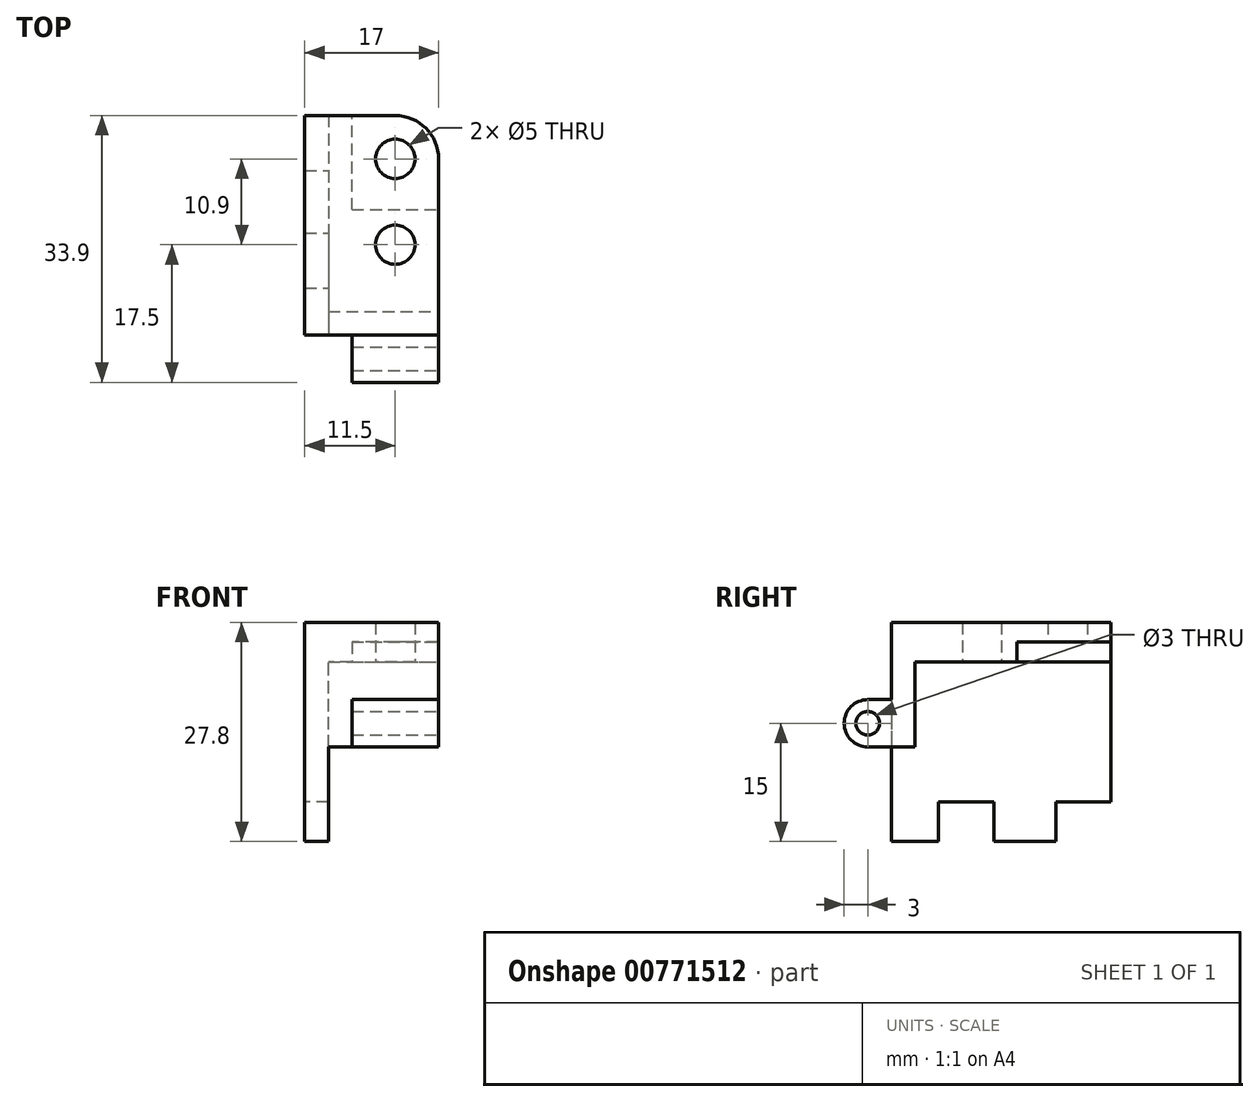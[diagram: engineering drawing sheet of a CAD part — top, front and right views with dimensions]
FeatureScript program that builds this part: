
annotation { "Feature Type Name" : "Feature", "Feature Type Description" : "" }
export const myFeature = defineFeature(function(context is Context, id is Id, definition is map)
    precondition{}
    {
        {
            var Q0;
            Q0=qCreatedBy(makeId("Top.planeOp"),FACE);
            var sketch = newSketch(context, id + "F0", { "sketchPlane" : qUnion([Q0])});
            skCircle(sketch, "E0", {"center": v(0, 0) * mm, "radius": 2.5 * mm});
            skLineSegment(sketch, "E1", {"start": v(0, 0) * mm, "end": v(-2.5, 0) * mm, "construction": true});
            skLineSegment(sketch, "E2", {"start": v(-2.5, 0) * mm, "end": v(2.5, 0) * mm, "construction": true});
            skArc(sketch, "E3", {"start": v(-5.5, 0) * mm, "mid": v(0, -5.5) * mm, "end": v(5.5, 0) * mm});
            skLineSegment(sketch, "E4", {"start": v(-5.5, 0) * mm, "end": v(-5.5, 10.9) * mm});
            skLineSegment(sketch, "E5", {"start": v(-2.5, 10.9) * mm, "end": v(2.5, 10.9) * mm});
            skLineSegment(sketch, "E6", {"start": v(5.5, 10.9) * mm, "end": v(5.5, 0) * mm});
            skCircle(sketch, "E7", {"center": v(0, 10.9) * mm, "radius": 2.5 * mm});
            skArc(sketch, "E8", {"start": v(-5.5, 10.9) * mm, "mid": v(0, 16.4) * mm, "end": v(5.5, 10.9) * mm});
            skLineSegment(sketch, "E9", {"start": v(-5.5, 5.45) * mm, "end": v(-5.5, 4.45) * mm});
            skLineSegment(sketch, "E10", {"start": v(-5.5, 4.45) * mm, "end": v(5.5, 4.45) * mm});
            skLineSegment(sketch, "E11", {"start": v(0, 16.4) * mm, "end": v(-8.5, 16.4) * mm});
            skLineSegment(sketch, "E12", {"start": v(-8.5, 16.4) * mm, "end": v(-8.5, -5.5) * mm});
            skLineSegment(sketch, "E13", {"start": v(-8.5, -5.5) * mm, "end": v(0, -5.5) * mm});
            skLineSegment(sketch, "E14.bottom", {"start": v(-8.5, 16.4) * mm, "end": v(-11.5, 16.4) * mm});
            skLineSegment(sketch, "E14.top", {"start": v(-8.5, -5.5) * mm, "end": v(-11.5, -5.5) * mm});
            skLineSegment(sketch, "E14.right", {"start": v(-11.5, 16.4) * mm, "end": v(-11.5, -5.5) * mm});
            skLineSegment(sketch, "E15", {"start": v(-5.5, 10.9) * mm, "end": v(-5.5, 16.4) * mm});
            skLineSegment(sketch, "E16", {"start": v(5.5, 0) * mm, "end": v(5.5, -8.5) * mm});
            skLineSegment(sketch, "E17", {"start": v(-11.5, -5.5) * mm, "end": v(-11.5, -8.5) * mm});
            skLineSegment(sketch, "E18.bottom", {"start": v(-11.5, -8.5) * mm, "end": v(5.5, -8.5) * mm});
            skLineSegment(sketch, "E18.top", {"start": v(-11.5, -11.5) * mm, "end": v(5.5, -11.5) * mm});
            skLineSegment(sketch, "E18.left", {"start": v(-11.5, -8.5) * mm, "end": v(-11.5, -11.5) * mm});
            skLineSegment(sketch, "E18.right", {"start": v(5.5, -8.5) * mm, "end": v(5.5, -11.5) * mm});
            skLineSegment(sketch, "E19", {"start": v(-8.5, -5.5) * mm, "end": v(-8.5, -8.5) * mm});
            skLineSegment(sketch, "E20", {"start": v(-8.5, -8.5) * mm, "end": v(-8.5, -11.5) * mm});
            skSolve(sketch);
        }
        {
            var Q0;
            Q0=makeQuery(id+"F0.imprint","IMPRINT",FACE,{"disambiguationData":[TD([[makeQuery(id+"F0.imprint","IMPRINT",EDGE,{"derivedFrom":sQuery(id+"F0.wireOp",EDGE,"E0")}),-1.0]])]});
            var Q1;
            {var subQ7=sQuery(id+"F0.wireOp",EDGE,"E10");Q1=makeQuery(id+"F0.imprint","IMPRINT",FACE,{"disambiguationData":[TD([[makeQuery(id+"F0.imprint","IMPRINT",EDGE,{"derivedFrom":subQ7}),1.0]])]});}
            var Q2;
            {var subQ3=sQuery(id+"F0.wireOp",EDGE,"E12");Q2=makeQuery(id+"F0.imprint","IMPRINT",FACE,{"disambiguationData":[TD([[makeQuery(id+"F0.imprint","IMPRINT",EDGE,{"derivedFrom":subQ3}),1.0]])]});}
            var Q3;
            {var subQ0=sQuery(id+"F0.wireOp",EDGE,"E15");Q3=makeQuery(id+"F0.imprint","IMPRINT",FACE,{"disambiguationData":[TD([[makeQuery(id+"F0.imprint","IMPRINT",EDGE,{"derivedFrom":subQ0}),-1.0]])]});}
            var Q4;
            {var subQ4=sQuery(id+"F0.wireOp",EDGE,"E13");Q4=makeQuery(id+"F0.imprint","IMPRINT",FACE,{"disambiguationData":[TD([[makeQuery(id+"F0.imprint","IMPRINT",EDGE,{"derivedFrom":subQ4}),-1.0]])]});}
            var Q5;
            {var subQ0=sQuery(id+"F0.wireOp",EDGE,"E18.right");var subQ7=sQuery(id+"F0.wireOp",EDGE,"E18.left");Q5=qUnion([makeQuery(id+"F0.imprint","IMPRINT",FACE,{"disambiguationData":[TD([[makeQuery(id+"F0.imprint","IMPRINT",EDGE,{"derivedFrom":subQ7}),1.0]])]}),makeQuery(id+"F0.imprint","IMPRINT",FACE,{"disambiguationData":[TD([[makeQuery(id+"F0.imprint","IMPRINT",EDGE,{"derivedFrom":subQ0}),-1.0]])]})]);}
            extrude(context, id + "F1", {"entities" : qUnion([Q0, Q1, Q2, Q3, Q4, Q5]), "depth" : 5 * mm, "offsetDistance" : 25 * mm});
        }
        {
            var Q0;
            {var subQ7=sQuery(id+"F0.wireOp",EDGE,"E10");Q0=makeQuery(id+"F0.imprint","IMPRINT",FACE,{"disambiguationData":[TD([[makeQuery(id+"F0.imprint","IMPRINT",EDGE,{"derivedFrom":subQ7}),1.0]])]});}
            var Q1;
            {var subQ0=sQuery(id+"F0.wireOp",EDGE,"E15");Q1=makeQuery(id+"F0.imprint","IMPRINT",FACE,{"disambiguationData":[TD([[makeQuery(id+"F0.imprint","IMPRINT",EDGE,{"derivedFrom":subQ0}),-1.0]])]});}
            extrude(context, id + "F2", {"entities" : qUnion([Q0, Q1]), "operationType" : NewBodyOperationType.REMOVE, "depth" : 2.5 * mm, "offsetDistance" : 25 * mm});
        }
        {
            var Q0;
            {var subQ0=sQuery(id+"F0.wireOp",EDGE,"E18.left");Q0=makeQuery(id+"F0.imprint","IMPRINT",FACE,{"disambiguationData":[TD([[makeQuery(id+"F0.imprint","IMPRINT",EDGE,{"derivedFrom":subQ0}),1.0]])]});}
            var Q1;
            Q1=makeQuery(id+"F0.imprint","IMPRINT",FACE,{"disambiguationData":[TD([[makeQuery(id+"F0.imprint","IMPRINT",EDGE,{"derivedFrom":sQuery(id+"F0.wireOp",EDGE,"E12")}),-1.0]])]});
            var Q2;
            Q2=makeQuery(id+"F0.imprint","IMPRINT",FACE,{"disambiguationData":[TD([[makeQuery(id+"F0.imprint","IMPRINT",EDGE,{"derivedFrom":sQuery(id+"F0.wireOp",EDGE,"E14.top")}),1.0]])]});
            extrude(context, id + "F3", {"entities" : qUnion([Q0, Q1, Q2]), "operationType" : NewBodyOperationType.ADD, "oppositeDirection" : true, "depth" : 22.8 * mm, "offsetDistance" : 25 * mm, "hasSecondDirection" : true, "secondDirectionOppositeDirection" : false, "secondDirectionDepth" : 5 * mm});
        }
        {
            var Q0;
            Q0=makeQuery(id+"F3.opExtrude","CAP_FACE",FACE,{"disambiguationData":[OSD([sQuery(id+"F0.wireOp",EDGE,"E12"),sQuery(id+"F0.wireOp",EDGE,"E14.bottom"),sQuery(id+"F0.wireOp",EDGE,"E14.right"),sQuery(id+"F0.wireOp",EDGE,"E17"),sQuery(id+"F0.wireOp",EDGE,"E18.top"),sQuery(id+"F0.wireOp",EDGE,"E18.left"),sQuery(id+"F0.wireOp",EDGE,"E19"),sQuery(id+"F0.wireOp",EDGE,"E20")])],"isStart":false});
            var sketch = newSketch(context, id + "F4", { "sketchPlane" : qUnion([Q0])});
            skLineSegment(sketch, "E21.bottom", {"start": v(-11.5, 5.5) * mm, "end": v(-8.5, 5.5) * mm});
            skLineSegment(sketch, "E21.top", {"start": v(-11.5, -1.5) * mm, "end": v(-8.5, -1.5) * mm});
            skLineSegment(sketch, "E21.left", {"start": v(-11.5, 5.5) * mm, "end": v(-11.5, -1.5) * mm});
            skLineSegment(sketch, "E21.right", {"start": v(-8.5, 5.5) * mm, "end": v(-8.5, -1.5) * mm});
            skLineSegment(sketch, "E22.bottom", {"start": v(-11.5, -16.4) * mm, "end": v(-8.5, -16.4) * mm});
            skLineSegment(sketch, "E22.top", {"start": v(-11.5, -9.4) * mm, "end": v(-8.5, -9.4) * mm});
            skLineSegment(sketch, "E22.left", {"start": v(-11.5, -16.4) * mm, "end": v(-11.5, -9.4) * mm});
            skLineSegment(sketch, "E22.right", {"start": v(-8.5, -16.4) * mm, "end": v(-8.5, -9.4) * mm});
            skSolve(sketch);
        }
        {
            var Q0;
            Q0=makeQuery(id+"F4.imprint","IMPRINT",FACE,{"disambiguationData":[TD([[makeQuery(id+"F4.imprint","IMPRINT",EDGE,{"derivedFrom":sQuery(id+"F4.wireOp",EDGE,"E22.bottom")}),-1.0]])]});
            var Q1;
            Q1=makeQuery(id+"F4.imprint","IMPRINT",FACE,{"disambiguationData":[TD([[makeQuery(id+"F4.imprint","IMPRINT",EDGE,{"derivedFrom":sQuery(id+"F4.wireOp",EDGE,"E21.bottom")}),-1.0]])]});
            extrude(context, id + "F5", {"entities" : qUnion([Q0, Q1]), "operationType" : NewBodyOperationType.REMOVE, "oppositeDirection" : true, "depth" : 5 * mm, "offsetDistance" : 25 * mm});
        }
        {
            var Q0;
            {var subQ0=sQuery(id+"F0.wireOp",EDGE,"E18.right");Q0=makeQuery(id+"F0.imprint","IMPRINT",FACE,{"disambiguationData":[TD([[makeQuery(id+"F0.imprint","IMPRINT",EDGE,{"derivedFrom":subQ0}),-1.0]])]});}
            extrude(context, id + "F6", {"entities" : qUnion([Q0]), "operationType" : NewBodyOperationType.ADD, "oppositeDirection" : true, "depth" : 10.8 * mm, "offsetDistance" : 25 * mm});
        }
        {
            var Q0;
            {var subQ0=sQuery(id+"F0.wireOp",EDGE,"E18.right");Q0=makeQuery(id+"F6.boolean.opBoolean","MERGE",FACE,{"derivedFrom":[makeQuery(id+"F1.opExtrude","SWEPT_FACE",FACE,{"disambiguationData":[OSD([sQuery(id+"F0.wireOp",EDGE,"E6"),sQuery(id+"F0.wireOp",EDGE,"E16"),subQ0])]}),makeQuery(id+"F6.opExtrude","SWEPT_FACE",FACE,{"disambiguationData":[OSD([subQ0])]})]});}
            var sketch = newSketch(context, id + "F7", { "sketchPlane" : qUnion([Q0])});
            skLineSegment(sketch, "E23", {"start": v(-11.5, -10.8) * mm, "end": v(-14.5, -10.8) * mm});
            skLineSegment(sketch, "E24", {"start": v(-14.5, -10.8) * mm, "end": v(-14.5, -7.8) * mm});
            skCircle(sketch, "E25", {"center": v(-14.5, -7.8) * mm, "radius": 1.5 * mm});
            skCircle(sketch, "E26", {"center": v(-14.5, -7.8) * mm, "radius": 3 * mm});
            skLineSegment(sketch, "E27", {"start": v(-14.5, -7.8) * mm, "end": v(-14.5, -4.8) * mm});
            skLineSegment(sketch, "E28", {"start": v(-14.5, -4.8) * mm, "end": v(-11.5, -4.8) * mm});
            skSolve(sketch);
        }
        {
            var Q0;
            {var subQ1=sQuery(id+"F7.wireOp",EDGE,"E24");var subQ3=sQuery(id+"F7.wireOp",EDGE,"E25");var subQ4=makeQuery(id+"F7.imprint","INTERSECT",VERTEX,{"derivedFrom":[subQ1,subQ3]});Q0=makeQuery(id+"F7.imprint","IMPRINT",FACE,{"disambiguationData":[TD([[makeQuery(id+"F7.imprint","IMPRINT",EDGE,{"disambiguationData":[TD([[subQ4,1.0]])],"derivedFrom":subQ3}),-1.0]])]});}
            var Q1;
            {var subQ1=sQuery(id+"F7.wireOp",EDGE,"E24");var subQ8=sQuery(id+"F7.wireOp",EDGE,"E25");var subQ9=makeQuery(id+"F7.imprint","INTERSECT",VERTEX,{"derivedFrom":[subQ1,subQ8]});Q1=makeQuery(id+"F7.imprint","IMPRINT",FACE,{"disambiguationData":[TD([[makeQuery(id+"F7.imprint","IMPRINT",EDGE,{"disambiguationData":[TD([[subQ9,-1.0]])],"derivedFrom":subQ8}),-1.0]])]});}
            var Q2;
            {var subQ0=sQuery(id+"F7.wireOp",EDGE,"E28");Q2=makeQuery(id+"F7.imprint","IMPRINT",FACE,{"disambiguationData":[TD([[makeQuery(id+"F7.imprint","IMPRINT",EDGE,{"derivedFrom":subQ0}),-1.0]])]});}
            var Q3;
            {var subQ0=sQuery(id+"F7.wireOp",EDGE,"E23");Q3=makeQuery(id+"F7.imprint","IMPRINT",FACE,{"disambiguationData":[TD([[makeQuery(id+"F7.imprint","IMPRINT",EDGE,{"derivedFrom":subQ0}),-1.0]])]});}
            extrude(context, id + "F8", {"entities" : qUnion([Q0, Q1, Q2, Q3]), "operationType" : NewBodyOperationType.ADD, "oppositeDirection" : true, "depth" : 11 * mm, "offsetDistance" : 25 * mm});
        }
    });
